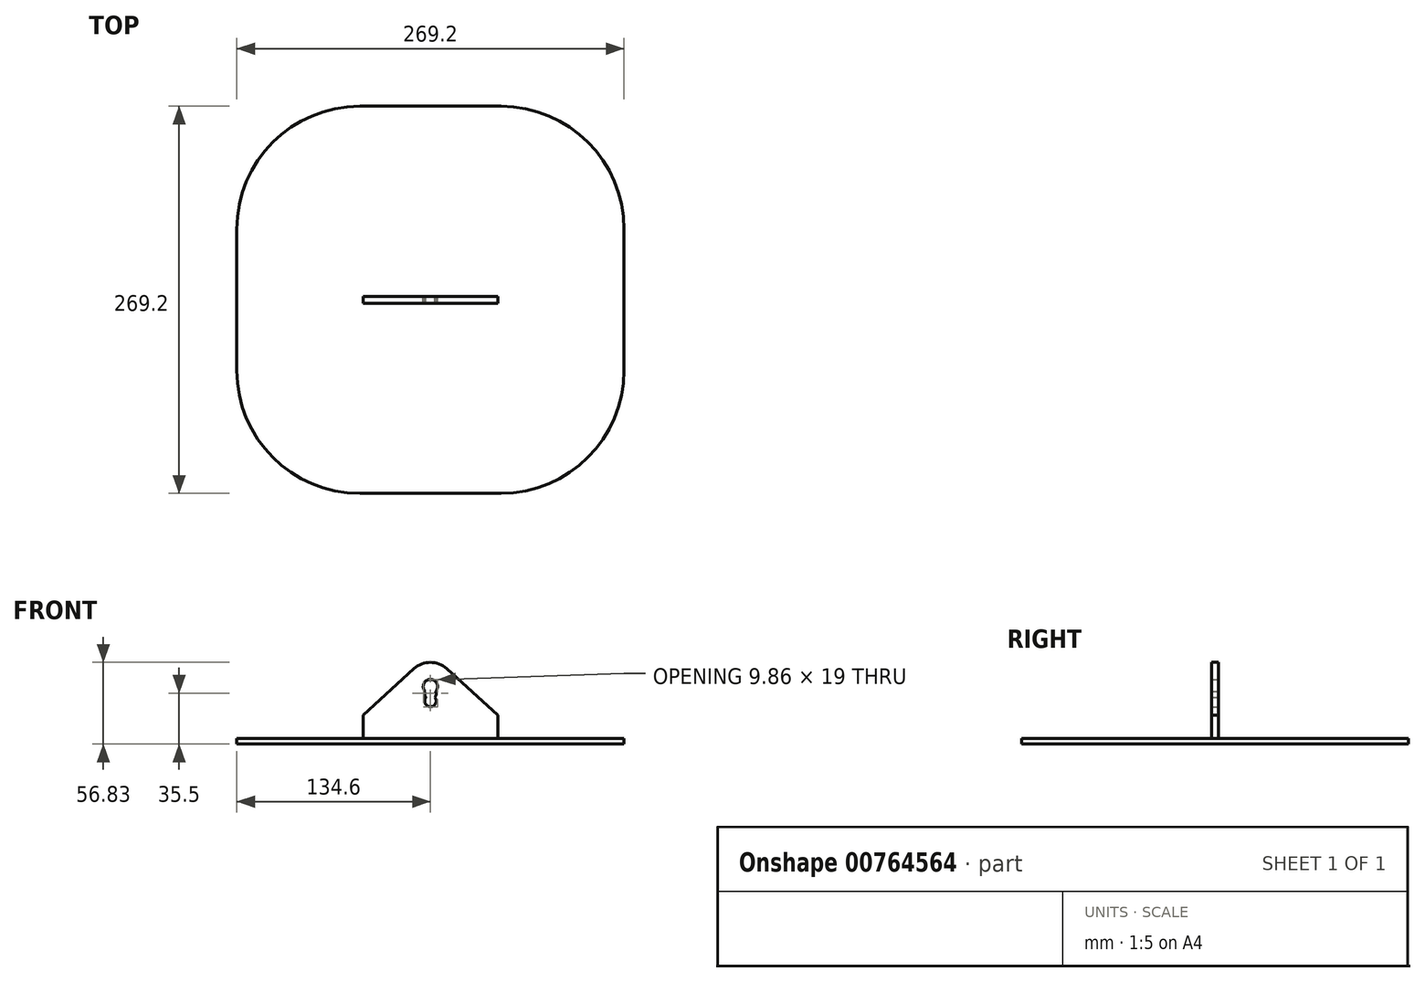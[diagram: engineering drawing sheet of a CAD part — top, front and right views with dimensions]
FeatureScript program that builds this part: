
annotation { "Feature Type Name" : "Feature", "Feature Type Description" : "" }
export const myFeature = defineFeature(function(context is Context, id is Id, definition is map)
    precondition{}
    {
        {
            var Q0;
            Q0=qCreatedBy(makeId("Top.planeOp"),FACE);
            var sketch = newSketch(context, id + "F0", { "sketchPlane" : qUnion([Q0])});
            skLineSegment(sketch, "E0.bottom", {"start": v(-49.1, 134.6) * mm, "end": v(49.1, 134.6) * mm});
            skLineSegment(sketch, "E0.top", {"start": v(-49.1, -134.6) * mm, "end": v(49.1, -134.6) * mm});
            skLineSegment(sketch, "E0.left", {"start": v(-134.6, 49.1) * mm, "end": v(-134.6, -49.1) * mm});
            skLineSegment(sketch, "E0.right", {"start": v(134.6, 49.1) * mm, "end": v(134.6, -49.1) * mm});
            skPoint(sketch, "E1.visualSharp", {"position": v(134.6, 134.6) * mm});
            skArc(sketch, "E1.filletArc", {"start": v(134.6, 49.1) * mm, "mid": v(109.56, 109.56) * mm, "end": v(49.1, 134.6) * mm});
            skPoint(sketch, "E2.visualSharp", {"position": v(134.6, -134.6) * mm});
            skArc(sketch, "E2.filletArc", {"start": v(49.1, -134.6) * mm, "mid": v(109.56, -109.56) * mm, "end": v(134.6, -49.1) * mm});
            skPoint(sketch, "E3.visualSharp", {"position": v(-134.6, -134.6) * mm});
            skArc(sketch, "E3.filletArc", {"start": v(-134.6, -49.1) * mm, "mid": v(-109.56, -109.56) * mm, "end": v(-49.1, -134.6) * mm});
            skPoint(sketch, "E4.visualSharp", {"position": v(-134.6, 134.6) * mm});
            skArc(sketch, "E4.filletArc", {"start": v(-49.1, 134.6) * mm, "mid": v(-109.56, 109.56) * mm, "end": v(-134.6, 49.1) * mm});
            skSolve(sketch);
        }
        {
            var Q0;
            Q0 = qSketchRegion(id + "F0", true);
            extrude(context, id + "F1", {"entities" : qUnion([Q0]), "endBound" : BoundingType.SYMMETRIC, "depth" : 4 * mm, "offsetDistance" : 25 * mm});
        }
        {
            var Q0;
            Q0=qCreatedBy(makeId("Front.planeOp"),FACE);
            var sketch = newSketch(context, id + "F2", { "sketchPlane" : qUnion([Q0])});
            skCircle(sketch, "E5", {"center": v(0, 38) * mm, "radius": 5 * mm});
            skLineSegment(sketch, "E6", {"start": v(0, 0) * mm, "end": v(-46.87, 0) * mm});
            skLineSegment(sketch, "E7", {"start": v(-46.87, 0) * mm, "end": v(-46.87, 18.03) * mm});
            skArc(sketch, "E8", {"start": v(11.34, 50.44) * mm, "mid": v(0, 54.83) * mm, "end": v(-11.34, 50.44) * mm});
            skLineSegment(sketch, "E9", {"start": v(-46.87, 18.03) * mm, "end": v(-11.34, 50.44) * mm});
            skLineSegment(sketch, "E10.MirrorCS", {"start": v(46.87, 18.03) * mm, "end": v(11.34, 50.44) * mm});
            skLineSegment(sketch, "E11.MirrorCS", {"start": v(46.87, 0) * mm, "end": v(46.87, 18.03) * mm});
            skLineSegment(sketch, "E12.MirrorCS", {"start": v(0, 0) * mm, "end": v(46.87, 0) * mm});
            skCircle(sketch, "E13", {"center": v(0, 33) * mm, "radius": 4 * mm});
            skCircle(sketch, "E14", {"center": v(0, 28) * mm, "radius": 4 * mm});
            skSolve(sketch);
        }
        {
            var Q0;
            Q0 = qSketchRegion(id + "F2", true);
            extrude(context, id + "F3", {"entities" : qUnion([Q0]), "operationType" : NewBodyOperationType.ADD, "endBound" : BoundingType.SYMMETRIC, "depth" : 5 * mm, "offsetDistance" : 25 * mm});
        }
    });
